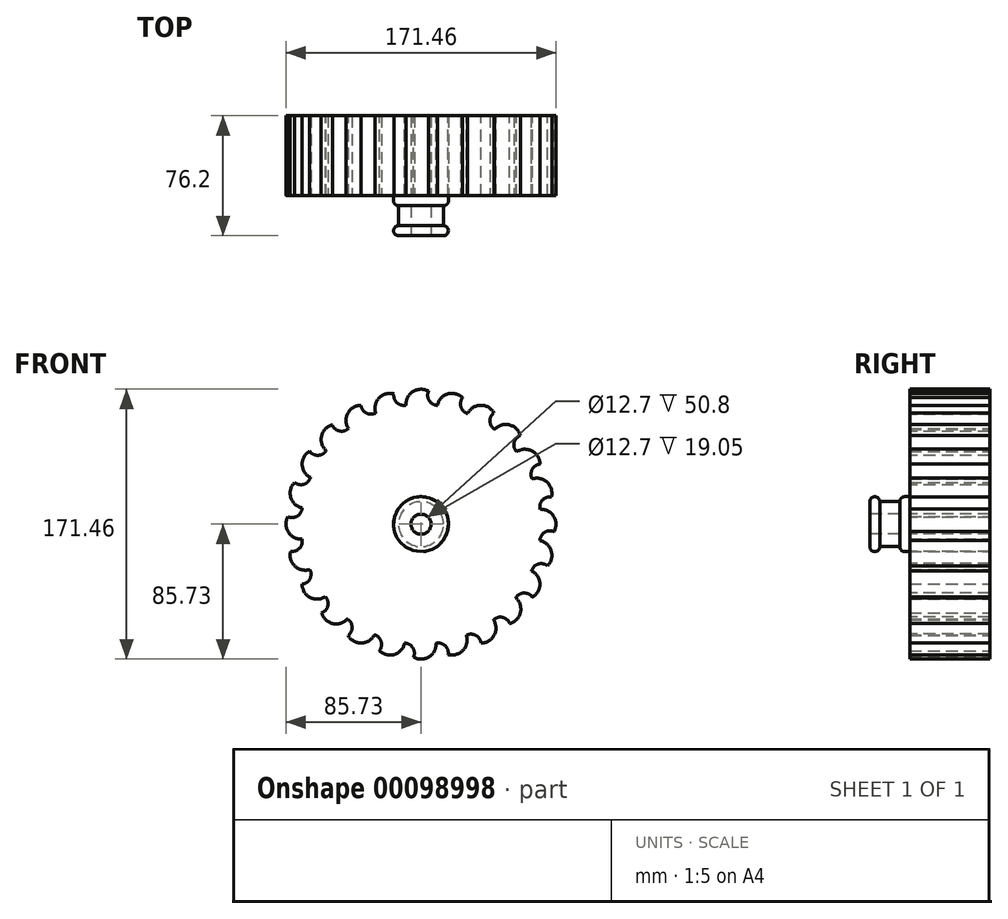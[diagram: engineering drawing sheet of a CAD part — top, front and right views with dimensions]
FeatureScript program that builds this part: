
annotation { "Feature Type Name" : "Feature", "Feature Type Description" : "" }
export const myFeature = defineFeature(function(context is Context, id is Id, definition is map)
    precondition{}
    {
        {
            var Q0;
            Q0=qCreatedBy(makeId("Front.planeOp"),FACE);
            var sketch = newSketch(context, id + "F0", { "sketchPlane" : qUnion([Q0])});
            skArc(sketch, "E0", {"start": v(-9.5, 75.6) * mm, "mid": v(4.76, -76.05) * mm, "end": v(0, 76.2) * mm});
            skArc(sketch, "E1", {"start": v(4.76, 84.45) * mm, "mid": v(-5.02, 84.3) * mm, "end": v(-9.5, 75.6) * mm});
            skLineSegment(sketch, "E2", {"start": v(0, 0) * mm, "end": v(0, 76.2) * mm, "construction": true});
            skLineSegment(sketch, "E3", {"start": v(0, 0) * mm, "end": v(39.83, 0) * mm, "construction": true});
            skLineSegment(sketch, "E4", {"start": v(0, 76.2) * mm, "end": v(4.76, 84.45) * mm});
            skArc(sketch, "E5.1.0", {"start": v(-17.26, 82.8) * mm, "mid": v(-26.66, 80.12) * mm, "end": v(-28.75, 70.57) * mm});
            skLineSegment(sketch, "E5.1.1", {"start": v(-19.72, 73.6) * mm, "end": v(-17.26, 82.8) * mm});
            skArc(sketch, "E5.2.0", {"start": v(-38.1, 75.52) * mm, "mid": v(-46.5, 70.5) * mm, "end": v(-46.04, 60.72) * mm});
            skLineSegment(sketch, "E5.2.1", {"start": v(-38.1, 66) * mm, "end": v(-38.1, 75.52) * mm});
            skArc(sketch, "E5.3.0", {"start": v(-56.35, 63.08) * mm, "mid": v(-63.15, 56.06) * mm, "end": v(-60.18, 46.74) * mm});
            skLineSegment(sketch, "E5.3.1", {"start": v(-53.88, 53.88) * mm, "end": v(-56.35, 63.08) * mm});
            skArc(sketch, "E5.4.0", {"start": v(-70.75, 46.35) * mm, "mid": v(-75.51, 37.8) * mm, "end": v(-70.23, 29.57) * mm});
            skLineSegment(sketch, "E5.4.1", {"start": v(-66, 38.1) * mm, "end": v(-70.75, 46.35) * mm});
            skArc(sketch, "E5.5.0", {"start": v(-80.34, 26.46) * mm, "mid": v(-82.72, 16.97) * mm, "end": v(-75.49, 10.39) * mm});
            skLineSegment(sketch, "E5.5.1", {"start": v(-73.6, 19.72) * mm, "end": v(-80.34, 26.46) * mm});
            skArc(sketch, "E5.6.0", {"start": v(-84.45, 4.76) * mm, "mid": v(-84.3, -5.02) * mm, "end": v(-75.6, -9.5) * mm});
            skLineSegment(sketch, "E5.6.1", {"start": v(-76.2, 0) * mm, "end": v(-84.45, 4.76) * mm});
            skArc(sketch, "E5.7.0", {"start": v(-82.8, -17.26) * mm, "mid": v(-80.12, -26.66) * mm, "end": v(-70.57, -28.75) * mm});
            skLineSegment(sketch, "E5.7.1", {"start": v(-73.6, -19.72) * mm, "end": v(-82.8, -17.26) * mm});
            skArc(sketch, "E5.8.0", {"start": v(-75.52, -38.1) * mm, "mid": v(-70.5, -46.5) * mm, "end": v(-60.72, -46.04) * mm});
            skLineSegment(sketch, "E5.8.1", {"start": v(-66, -38.1) * mm, "end": v(-75.52, -38.1) * mm});
            skArc(sketch, "E5.9.0", {"start": v(-63.08, -56.35) * mm, "mid": v(-56.06, -63.15) * mm, "end": v(-46.74, -60.18) * mm});
            skLineSegment(sketch, "E5.9.1", {"start": v(-53.88, -53.88) * mm, "end": v(-63.08, -56.35) * mm});
            skArc(sketch, "E5.10.0", {"start": v(-46.35, -70.75) * mm, "mid": v(-37.8, -75.51) * mm, "end": v(-29.57, -70.23) * mm});
            skLineSegment(sketch, "E5.10.1", {"start": v(-38.1, -66) * mm, "end": v(-46.35, -70.75) * mm});
            skArc(sketch, "E5.11.0", {"start": v(-26.46, -80.34) * mm, "mid": v(-16.97, -82.72) * mm, "end": v(-10.39, -75.49) * mm});
            skLineSegment(sketch, "E5.11.1", {"start": v(-19.72, -73.6) * mm, "end": v(-26.46, -80.34) * mm});
            skArc(sketch, "E5.12.0", {"start": v(-4.76, -84.45) * mm, "mid": v(5.02, -84.3) * mm, "end": v(9.5, -75.6) * mm});
            skLineSegment(sketch, "E5.12.1", {"start": v(0, -76.2) * mm, "end": v(-4.76, -84.45) * mm});
            skArc(sketch, "E5.13.0", {"start": v(17.26, -82.8) * mm, "mid": v(26.66, -80.12) * mm, "end": v(28.75, -70.57) * mm});
            skLineSegment(sketch, "E5.13.1", {"start": v(19.72, -73.6) * mm, "end": v(17.26, -82.8) * mm});
            skArc(sketch, "E5.14.0", {"start": v(38.1, -75.52) * mm, "mid": v(46.5, -70.5) * mm, "end": v(46.04, -60.72) * mm});
            skLineSegment(sketch, "E5.14.1", {"start": v(38.1, -66) * mm, "end": v(38.1, -75.52) * mm});
            skArc(sketch, "E5.15.0", {"start": v(56.35, -63.08) * mm, "mid": v(63.15, -56.06) * mm, "end": v(60.18, -46.74) * mm});
            skLineSegment(sketch, "E5.15.1", {"start": v(53.88, -53.88) * mm, "end": v(56.35, -63.08) * mm});
            skArc(sketch, "E5.16.0", {"start": v(70.75, -46.35) * mm, "mid": v(75.51, -37.8) * mm, "end": v(70.23, -29.57) * mm});
            skLineSegment(sketch, "E5.16.1", {"start": v(66, -38.1) * mm, "end": v(70.75, -46.35) * mm});
            skArc(sketch, "E5.17.0", {"start": v(80.34, -26.46) * mm, "mid": v(82.72, -16.97) * mm, "end": v(75.49, -10.39) * mm});
            skLineSegment(sketch, "E5.17.1", {"start": v(73.6, -19.72) * mm, "end": v(80.34, -26.46) * mm});
            skArc(sketch, "E5.18.0", {"start": v(84.45, -4.76) * mm, "mid": v(84.3, 5.02) * mm, "end": v(75.6, 9.5) * mm});
            skLineSegment(sketch, "E5.18.1", {"start": v(76.2, 0) * mm, "end": v(84.45, -4.76) * mm});
            skArc(sketch, "E5.19.0", {"start": v(82.8, 17.26) * mm, "mid": v(80.12, 26.66) * mm, "end": v(70.57, 28.75) * mm});
            skLineSegment(sketch, "E5.19.1", {"start": v(73.6, 19.72) * mm, "end": v(82.8, 17.26) * mm});
            skArc(sketch, "E5.20.0", {"start": v(75.52, 38.1) * mm, "mid": v(70.5, 46.5) * mm, "end": v(60.72, 46.04) * mm});
            skLineSegment(sketch, "E5.20.1", {"start": v(66, 38.1) * mm, "end": v(75.52, 38.1) * mm});
            skArc(sketch, "E5.21.0", {"start": v(63.08, 56.35) * mm, "mid": v(56.06, 63.15) * mm, "end": v(46.74, 60.18) * mm});
            skLineSegment(sketch, "E5.21.1", {"start": v(53.88, 53.88) * mm, "end": v(63.08, 56.35) * mm});
            skArc(sketch, "E5.22.0", {"start": v(46.35, 70.75) * mm, "mid": v(37.8, 75.51) * mm, "end": v(29.57, 70.23) * mm});
            skLineSegment(sketch, "E5.22.1", {"start": v(38.1, 66) * mm, "end": v(46.35, 70.75) * mm});
            skArc(sketch, "E5.23.0", {"start": v(26.46, 80.34) * mm, "mid": v(16.97, 82.72) * mm, "end": v(10.39, 75.49) * mm});
            skLineSegment(sketch, "E5.23.1", {"start": v(19.72, 73.6) * mm, "end": v(26.46, 80.34) * mm});
            skSolve(sketch);
        }
        {
            var Q0;
            Q0 = qSketchRegion(id + "F0", true);
            extrude(context, id + "F1", {"entities" : qUnion([Q0]), "depth" : 50.8 * mm});
        }
        {
            var Q0;
            Q0=makeQuery(id+"F1.opExtrude","CAP_FACE",FACE,{"disambiguationData":[OSD([sQuery(id+"F0.wireOp",EDGE,"E0"),sQuery(id+"F0.wireOp",EDGE,"E1"),sQuery(id+"F0.wireOp",EDGE,"E4"),sQuery(id+"F0.wireOp",EDGE,"E5.1.0"),sQuery(id+"F0.wireOp",EDGE,"E5.1.1"),sQuery(id+"F0.wireOp",EDGE,"E5.2.0"),sQuery(id+"F0.wireOp",EDGE,"E5.2.1"),sQuery(id+"F0.wireOp",EDGE,"E5.3.0"),sQuery(id+"F0.wireOp",EDGE,"E5.3.1"),sQuery(id+"F0.wireOp",EDGE,"E5.4.0"),sQuery(id+"F0.wireOp",EDGE,"E5.4.1"),sQuery(id+"F0.wireOp",EDGE,"E5.5.0"),sQuery(id+"F0.wireOp",EDGE,"E5.5.1"),sQuery(id+"F0.wireOp",EDGE,"E5.6.0"),sQuery(id+"F0.wireOp",EDGE,"E5.6.1"),sQuery(id+"F0.wireOp",EDGE,"E5.7.0"),sQuery(id+"F0.wireOp",EDGE,"E5.7.1"),sQuery(id+"F0.wireOp",EDGE,"E5.8.0"),sQuery(id+"F0.wireOp",EDGE,"E5.8.1"),sQuery(id+"F0.wireOp",EDGE,"E5.9.0"),sQuery(id+"F0.wireOp",EDGE,"E5.9.1"),sQuery(id+"F0.wireOp",EDGE,"E5.10.0"),sQuery(id+"F0.wireOp",EDGE,"E5.10.1"),sQuery(id+"F0.wireOp",EDGE,"E5.11.0"),sQuery(id+"F0.wireOp",EDGE,"E5.11.1"),sQuery(id+"F0.wireOp",EDGE,"E5.12.0"),sQuery(id+"F0.wireOp",EDGE,"E5.12.1"),sQuery(id+"F0.wireOp",EDGE,"E5.13.0"),sQuery(id+"F0.wireOp",EDGE,"E5.13.1"),sQuery(id+"F0.wireOp",EDGE,"E5.14.0"),sQuery(id+"F0.wireOp",EDGE,"E5.14.1"),sQuery(id+"F0.wireOp",EDGE,"E5.15.0"),sQuery(id+"F0.wireOp",EDGE,"E5.15.1"),sQuery(id+"F0.wireOp",EDGE,"E5.16.0"),sQuery(id+"F0.wireOp",EDGE,"E5.16.1"),sQuery(id+"F0.wireOp",EDGE,"E5.17.0"),sQuery(id+"F0.wireOp",EDGE,"E5.17.1"),sQuery(id+"F0.wireOp",EDGE,"E5.18.0"),sQuery(id+"F0.wireOp",EDGE,"E5.18.1"),sQuery(id+"F0.wireOp",EDGE,"E5.19.0"),sQuery(id+"F0.wireOp",EDGE,"E5.19.1"),sQuery(id+"F0.wireOp",EDGE,"E5.20.0"),sQuery(id+"F0.wireOp",EDGE,"E5.20.1"),sQuery(id+"F0.wireOp",EDGE,"E5.21.0"),sQuery(id+"F0.wireOp",EDGE,"E5.21.1"),sQuery(id+"F0.wireOp",EDGE,"E5.22.0"),sQuery(id+"F0.wireOp",EDGE,"E5.22.1"),sQuery(id+"F0.wireOp",EDGE,"E5.23.0"),sQuery(id+"F0.wireOp",EDGE,"E5.23.1")])],"isStart":false});
            var sketch = newSketch(context, id + "F2", { "sketchPlane" : qUnion([Q0])});
            skPoint(sketch, "E6", {"position": v(0, 0) * mm});
            skPoint(sketch, "E7", {"position": v(0, 0.1) * mm});
            skSolve(sketch);
        }
        {
            var Q0;
            Q0=sQuery(id+"F2.wireOp",VERTEX,"E6");
            var Q1;
            Q1=makeQuery(id+"F1.opExtrude","SWEPT_BODY",BODY,{"disambiguationData":[OSD([sQuery(id+"F0.wireOp",EDGE,"E0"),sQuery(id+"F0.wireOp",EDGE,"E1"),sQuery(id+"F0.wireOp",EDGE,"E4"),sQuery(id+"F0.wireOp",EDGE,"E5.1.0"),sQuery(id+"F0.wireOp",EDGE,"E5.1.1"),sQuery(id+"F0.wireOp",EDGE,"E5.2.0"),sQuery(id+"F0.wireOp",EDGE,"E5.2.1"),sQuery(id+"F0.wireOp",EDGE,"E5.3.0"),sQuery(id+"F0.wireOp",EDGE,"E5.3.1"),sQuery(id+"F0.wireOp",EDGE,"E5.4.0"),sQuery(id+"F0.wireOp",EDGE,"E5.4.1"),sQuery(id+"F0.wireOp",EDGE,"E5.5.0"),sQuery(id+"F0.wireOp",EDGE,"E5.5.1"),sQuery(id+"F0.wireOp",EDGE,"E5.6.0"),sQuery(id+"F0.wireOp",EDGE,"E5.6.1"),sQuery(id+"F0.wireOp",EDGE,"E5.7.0"),sQuery(id+"F0.wireOp",EDGE,"E5.7.1"),sQuery(id+"F0.wireOp",EDGE,"E5.8.0"),sQuery(id+"F0.wireOp",EDGE,"E5.8.1"),sQuery(id+"F0.wireOp",EDGE,"E5.9.0"),sQuery(id+"F0.wireOp",EDGE,"E5.9.1"),sQuery(id+"F0.wireOp",EDGE,"E5.10.0"),sQuery(id+"F0.wireOp",EDGE,"E5.10.1"),sQuery(id+"F0.wireOp",EDGE,"E5.11.0"),sQuery(id+"F0.wireOp",EDGE,"E5.11.1"),sQuery(id+"F0.wireOp",EDGE,"E5.12.0"),sQuery(id+"F0.wireOp",EDGE,"E5.12.1"),sQuery(id+"F0.wireOp",EDGE,"E5.13.0"),sQuery(id+"F0.wireOp",EDGE,"E5.13.1"),sQuery(id+"F0.wireOp",EDGE,"E5.14.0"),sQuery(id+"F0.wireOp",EDGE,"E5.14.1"),sQuery(id+"F0.wireOp",EDGE,"E5.15.0"),sQuery(id+"F0.wireOp",EDGE,"E5.15.1"),sQuery(id+"F0.wireOp",EDGE,"E5.16.0"),sQuery(id+"F0.wireOp",EDGE,"E5.16.1"),sQuery(id+"F0.wireOp",EDGE,"E5.17.0"),sQuery(id+"F0.wireOp",EDGE,"E5.17.1"),sQuery(id+"F0.wireOp",EDGE,"E5.18.0"),sQuery(id+"F0.wireOp",EDGE,"E5.18.1"),sQuery(id+"F0.wireOp",EDGE,"E5.19.0"),sQuery(id+"F0.wireOp",EDGE,"E5.19.1"),sQuery(id+"F0.wireOp",EDGE,"E5.20.0"),sQuery(id+"F0.wireOp",EDGE,"E5.20.1"),sQuery(id+"F0.wireOp",EDGE,"E5.21.0"),sQuery(id+"F0.wireOp",EDGE,"E5.21.1"),sQuery(id+"F0.wireOp",EDGE,"E5.22.0"),sQuery(id+"F0.wireOp",EDGE,"E5.22.1"),sQuery(id+"F0.wireOp",EDGE,"E5.23.0"),sQuery(id+"F0.wireOp",EDGE,"E5.23.1")])]});
            hole(context, id + "F3", {"style" : HoleStyle.SIMPLE, "endStyle" : HoleEndStyle.THROUGH, "holeDiameter" : 12.7 * mm, "locations" : qUnion([Q0]), "scope" : qUnion([Q1]), "isTappedThrough" : true});
        }
        {
            var Q0;
            Q0=makeQuery(id+"F1.opExtrude","CAP_FACE",FACE,{"disambiguationData":[OSD([sQuery(id+"F0.wireOp",EDGE,"E0"),sQuery(id+"F0.wireOp",EDGE,"E1"),sQuery(id+"F0.wireOp",EDGE,"E4"),sQuery(id+"F0.wireOp",EDGE,"E5.1.0"),sQuery(id+"F0.wireOp",EDGE,"E5.1.1"),sQuery(id+"F0.wireOp",EDGE,"E5.2.0"),sQuery(id+"F0.wireOp",EDGE,"E5.2.1"),sQuery(id+"F0.wireOp",EDGE,"E5.3.0"),sQuery(id+"F0.wireOp",EDGE,"E5.3.1"),sQuery(id+"F0.wireOp",EDGE,"E5.4.0"),sQuery(id+"F0.wireOp",EDGE,"E5.4.1"),sQuery(id+"F0.wireOp",EDGE,"E5.5.0"),sQuery(id+"F0.wireOp",EDGE,"E5.5.1"),sQuery(id+"F0.wireOp",EDGE,"E5.6.0"),sQuery(id+"F0.wireOp",EDGE,"E5.6.1"),sQuery(id+"F0.wireOp",EDGE,"E5.7.0"),sQuery(id+"F0.wireOp",EDGE,"E5.7.1"),sQuery(id+"F0.wireOp",EDGE,"E5.8.0"),sQuery(id+"F0.wireOp",EDGE,"E5.8.1"),sQuery(id+"F0.wireOp",EDGE,"E5.9.0"),sQuery(id+"F0.wireOp",EDGE,"E5.9.1"),sQuery(id+"F0.wireOp",EDGE,"E5.10.0"),sQuery(id+"F0.wireOp",EDGE,"E5.10.1"),sQuery(id+"F0.wireOp",EDGE,"E5.11.0"),sQuery(id+"F0.wireOp",EDGE,"E5.11.1"),sQuery(id+"F0.wireOp",EDGE,"E5.12.0"),sQuery(id+"F0.wireOp",EDGE,"E5.12.1"),sQuery(id+"F0.wireOp",EDGE,"E5.13.0"),sQuery(id+"F0.wireOp",EDGE,"E5.13.1"),sQuery(id+"F0.wireOp",EDGE,"E5.14.0"),sQuery(id+"F0.wireOp",EDGE,"E5.14.1"),sQuery(id+"F0.wireOp",EDGE,"E5.15.0"),sQuery(id+"F0.wireOp",EDGE,"E5.15.1"),sQuery(id+"F0.wireOp",EDGE,"E5.16.0"),sQuery(id+"F0.wireOp",EDGE,"E5.16.1"),sQuery(id+"F0.wireOp",EDGE,"E5.17.0"),sQuery(id+"F0.wireOp",EDGE,"E5.17.1"),sQuery(id+"F0.wireOp",EDGE,"E5.18.0"),sQuery(id+"F0.wireOp",EDGE,"E5.18.1"),sQuery(id+"F0.wireOp",EDGE,"E5.19.0"),sQuery(id+"F0.wireOp",EDGE,"E5.19.1"),sQuery(id+"F0.wireOp",EDGE,"E5.20.0"),sQuery(id+"F0.wireOp",EDGE,"E5.20.1"),sQuery(id+"F0.wireOp",EDGE,"E5.21.0"),sQuery(id+"F0.wireOp",EDGE,"E5.21.1"),sQuery(id+"F0.wireOp",EDGE,"E5.22.0"),sQuery(id+"F0.wireOp",EDGE,"E5.22.1"),sQuery(id+"F0.wireOp",EDGE,"E5.23.0"),sQuery(id+"F0.wireOp",EDGE,"E5.23.1")])],"isStart":false});
            var sketch = newSketch(context, id + "F4", { "sketchPlane" : qUnion([Q0])});
            skCircle(sketch, "E8", {"center": v(0, 0) * mm, "radius": 14.29 * mm});
            skSolve(sketch);
        }
        {
            var Q0;
            Q0=makeQuery(id+"F4.imprint","IMPRINT",FACE,{"disambiguationData":[TD([[makeQuery(id+"F4.imprint","IMPRINT",EDGE,{"derivedFrom":sQuery(id+"F4.wireOp",EDGE,"E8")}),1.0]])]});
            extrude(context, id + "F5", {"entities" : qUnion([Q0]), "operationType" : NewBodyOperationType.ADD, "depth" : 25.4 * mm});
        }
        {
            var Q0;
            Q0=makeQuery(id+"F1.opExtrude","CAP_FACE",FACE,{"disambiguationData":[OSD([sQuery(id+"F0.wireOp",EDGE,"E0"),sQuery(id+"F0.wireOp",EDGE,"E1"),sQuery(id+"F0.wireOp",EDGE,"E4"),sQuery(id+"F0.wireOp",EDGE,"E5.1.0"),sQuery(id+"F0.wireOp",EDGE,"E5.1.1"),sQuery(id+"F0.wireOp",EDGE,"E5.2.0"),sQuery(id+"F0.wireOp",EDGE,"E5.2.1"),sQuery(id+"F0.wireOp",EDGE,"E5.3.0"),sQuery(id+"F0.wireOp",EDGE,"E5.3.1"),sQuery(id+"F0.wireOp",EDGE,"E5.4.0"),sQuery(id+"F0.wireOp",EDGE,"E5.4.1"),sQuery(id+"F0.wireOp",EDGE,"E5.5.0"),sQuery(id+"F0.wireOp",EDGE,"E5.5.1"),sQuery(id+"F0.wireOp",EDGE,"E5.6.0"),sQuery(id+"F0.wireOp",EDGE,"E5.6.1"),sQuery(id+"F0.wireOp",EDGE,"E5.7.0"),sQuery(id+"F0.wireOp",EDGE,"E5.7.1"),sQuery(id+"F0.wireOp",EDGE,"E5.8.0"),sQuery(id+"F0.wireOp",EDGE,"E5.8.1"),sQuery(id+"F0.wireOp",EDGE,"E5.9.0"),sQuery(id+"F0.wireOp",EDGE,"E5.9.1"),sQuery(id+"F0.wireOp",EDGE,"E5.10.0"),sQuery(id+"F0.wireOp",EDGE,"E5.10.1"),sQuery(id+"F0.wireOp",EDGE,"E5.11.0"),sQuery(id+"F0.wireOp",EDGE,"E5.11.1"),sQuery(id+"F0.wireOp",EDGE,"E5.12.0"),sQuery(id+"F0.wireOp",EDGE,"E5.12.1"),sQuery(id+"F0.wireOp",EDGE,"E5.13.0"),sQuery(id+"F0.wireOp",EDGE,"E5.13.1"),sQuery(id+"F0.wireOp",EDGE,"E5.14.0"),sQuery(id+"F0.wireOp",EDGE,"E5.14.1"),sQuery(id+"F0.wireOp",EDGE,"E5.15.0"),sQuery(id+"F0.wireOp",EDGE,"E5.15.1"),sQuery(id+"F0.wireOp",EDGE,"E5.16.0"),sQuery(id+"F0.wireOp",EDGE,"E5.16.1"),sQuery(id+"F0.wireOp",EDGE,"E5.17.0"),sQuery(id+"F0.wireOp",EDGE,"E5.17.1"),sQuery(id+"F0.wireOp",EDGE,"E5.18.0"),sQuery(id+"F0.wireOp",EDGE,"E5.18.1"),sQuery(id+"F0.wireOp",EDGE,"E5.19.0"),sQuery(id+"F0.wireOp",EDGE,"E5.19.1"),sQuery(id+"F0.wireOp",EDGE,"E5.20.0"),sQuery(id+"F0.wireOp",EDGE,"E5.20.1"),sQuery(id+"F0.wireOp",EDGE,"E5.21.0"),sQuery(id+"F0.wireOp",EDGE,"E5.21.1"),sQuery(id+"F0.wireOp",EDGE,"E5.22.0"),sQuery(id+"F0.wireOp",EDGE,"E5.22.1"),sQuery(id+"F0.wireOp",EDGE,"E5.23.0"),sQuery(id+"F0.wireOp",EDGE,"E5.23.1")])],"isStart":false});
            var sketch = newSketch(context, id + "F6", { "sketchPlane" : qUnion([Q0])});
            skCircle(sketch, "E9", {"center": v(0, 0) * mm, "radius": 17.46 * mm});
            skSolve(sketch);
        }
        {
            var Q0;
            Q0 = qSketchRegion(id + "F6", true);
            extrude(context, id + "F7", {"entities" : qUnion([Q0]), "operationType" : NewBodyOperationType.ADD, "depth" : 6.35 * mm});
        }
        {
            var Q0;
            Q0=makeQuery(id+"F5.opExtrude","CAP_FACE",FACE,{"disambiguationData":[OSD([sQuery(id+"F3.hole-0.sketch.wireOp",EDGE,"core_line_2"),sQuery(id+"F3.hole-0.sketch.wireOp",EDGE,"core_line_3"),sQuery(id+"F4.wireOp",EDGE,"E8")])],"isStart":false});
            var sketch = newSketch(context, id + "F8", { "sketchPlane" : qUnion([Q0])});
            skCircle(sketch, "E10.0", {"center": v(0, 0) * mm, "radius": 17.46 * mm});
            skSolve(sketch);
        }
        {
            var Q0;
            Q0=makeQuery(id+"F8.imprint","IMPRINT",FACE,{"disambiguationData":[TD([[makeQuery(id+"F8.imprint","IMPRINT",EDGE,{"derivedFrom":sQuery(id+"F8.wireOp",EDGE,"E10.0")}),1.0]])]});
            extrude(context, id + "F9", {"entities" : qUnion([Q0]), "operationType" : NewBodyOperationType.ADD, "oppositeDirection" : true, "depth" : 6.35 * mm});
        }
        {
            var Q0;
            Q0=makeQuery(id+"F7.opExtrude","CAP_EDGE",EDGE,{"disambiguationData":[OSD([sQuery(id+"F6.wireOp",EDGE,"E9")])],"isStart":true});
            var Q1;
            Q1=makeQuery(id+"F9.opExtrude","CAP_EDGE",EDGE,{"disambiguationData":[OSD([sQuery(id+"F8.wireOp",EDGE,"E10.0")])],"isStart":true});
            var Q2;
            Q2=makeQuery(id+"F9.opExtrude","CAP_EDGE",EDGE,{"disambiguationData":[OSD([sQuery(id+"F8.wireOp",EDGE,"E10.0")])],"isStart":false});
            var Q3;
            Q3=makeQuery(id+"F7.opExtrude","CAP_EDGE",EDGE,{"disambiguationData":[OSD([sQuery(id+"F6.wireOp",EDGE,"E9")])],"isStart":false});
            fillet(context, id + "F10", {"entities" : qUnion([Q0, Q1, Q2, Q3]), "radius" : 3.17 * mm, "tangentPropagation" : true, "allowEdgeOverflow" : false});
        }
        {
            var Q0;
            Q0=makeQuery(id+"F1.opExtrude","SWEPT_EDGE",EDGE,{"disambiguationData":[OSD([sQuery(id+"F0.wireOp",EDGE,"E0"),sQuery(id+"F0.wireOp",EDGE,"E5.20.1")])]});
            var Q1;
            Q1=makeQuery(id+"F1.opExtrude","SWEPT_EDGE",EDGE,{"disambiguationData":[OSD([sQuery(id+"F0.wireOp",EDGE,"E0"),sQuery(id+"F0.wireOp",EDGE,"E5.21.1")])]});
            var Q2;
            Q2=makeQuery(id+"F1.opExtrude","SWEPT_EDGE",EDGE,{"disambiguationData":[OSD([sQuery(id+"F0.wireOp",EDGE,"E0"),sQuery(id+"F0.wireOp",EDGE,"E5.19.1")])]});
            var Q3;
            Q3=makeQuery(id+"F1.opExtrude","SWEPT_EDGE",EDGE,{"disambiguationData":[OSD([sQuery(id+"F0.wireOp",EDGE,"E0"),sQuery(id+"F0.wireOp",EDGE,"E5.18.1")])]});
            var Q4;
            Q4=makeQuery(id+"F1.opExtrude","SWEPT_EDGE",EDGE,{"disambiguationData":[OSD([sQuery(id+"F0.wireOp",EDGE,"E0"),sQuery(id+"F0.wireOp",EDGE,"E5.17.1")])]});
            var Q5;
            Q5=makeQuery(id+"F1.opExtrude","SWEPT_EDGE",EDGE,{"disambiguationData":[OSD([sQuery(id+"F0.wireOp",EDGE,"E0"),sQuery(id+"F0.wireOp",EDGE,"E5.16.1")])]});
            var Q6;
            Q6=makeQuery(id+"F1.opExtrude","SWEPT_EDGE",EDGE,{"disambiguationData":[OSD([sQuery(id+"F0.wireOp",EDGE,"E0"),sQuery(id+"F0.wireOp",EDGE,"E5.15.1")])]});
            var Q7;
            Q7=makeQuery(id+"F1.opExtrude","SWEPT_EDGE",EDGE,{"disambiguationData":[OSD([sQuery(id+"F0.wireOp",EDGE,"E0"),sQuery(id+"F0.wireOp",EDGE,"E5.14.1")])]});
            var Q8;
            Q8=makeQuery(id+"F1.opExtrude","SWEPT_EDGE",EDGE,{"disambiguationData":[OSD([sQuery(id+"F0.wireOp",EDGE,"E0"),sQuery(id+"F0.wireOp",EDGE,"E5.13.1")])]});
            var Q9;
            Q9=makeQuery(id+"F1.opExtrude","SWEPT_EDGE",EDGE,{"disambiguationData":[OSD([sQuery(id+"F0.wireOp",EDGE,"E0"),sQuery(id+"F0.wireOp",EDGE,"E5.12.1")])]});
            var Q10;
            Q10=makeQuery(id+"F1.opExtrude","SWEPT_EDGE",EDGE,{"disambiguationData":[OSD([sQuery(id+"F0.wireOp",EDGE,"E0"),sQuery(id+"F0.wireOp",EDGE,"E5.11.1")])]});
            var Q11;
            Q11=makeQuery(id+"F1.opExtrude","SWEPT_EDGE",EDGE,{"disambiguationData":[OSD([sQuery(id+"F0.wireOp",EDGE,"E0"),sQuery(id+"F0.wireOp",EDGE,"E5.10.1")])]});
            var Q12;
            Q12=makeQuery(id+"F1.opExtrude","SWEPT_EDGE",EDGE,{"disambiguationData":[OSD([sQuery(id+"F0.wireOp",EDGE,"E0"),sQuery(id+"F0.wireOp",EDGE,"E5.9.1")])]});
            var Q13;
            Q13=makeQuery(id+"F1.opExtrude","SWEPT_EDGE",EDGE,{"disambiguationData":[OSD([sQuery(id+"F0.wireOp",EDGE,"E0"),sQuery(id+"F0.wireOp",EDGE,"E5.8.1")])]});
            var Q14;
            Q14=makeQuery(id+"F1.opExtrude","SWEPT_EDGE",EDGE,{"disambiguationData":[OSD([sQuery(id+"F0.wireOp",EDGE,"E0"),sQuery(id+"F0.wireOp",EDGE,"E5.6.1")])]});
            var Q15;
            Q15=makeQuery(id+"F1.opExtrude","SWEPT_EDGE",EDGE,{"disambiguationData":[OSD([sQuery(id+"F0.wireOp",EDGE,"E0"),sQuery(id+"F0.wireOp",EDGE,"E5.7.1")])]});
            var Q16;
            Q16=makeQuery(id+"F1.opExtrude","SWEPT_EDGE",EDGE,{"disambiguationData":[OSD([sQuery(id+"F0.wireOp",EDGE,"E0"),sQuery(id+"F0.wireOp",EDGE,"E5.5.1")])]});
            var Q17;
            Q17=makeQuery(id+"F1.opExtrude","SWEPT_EDGE",EDGE,{"disambiguationData":[OSD([sQuery(id+"F0.wireOp",EDGE,"E0"),sQuery(id+"F0.wireOp",EDGE,"E5.4.1")])]});
            var Q18;
            Q18=makeQuery(id+"F1.opExtrude","SWEPT_EDGE",EDGE,{"disambiguationData":[OSD([sQuery(id+"F0.wireOp",EDGE,"E0"),sQuery(id+"F0.wireOp",EDGE,"E5.3.1")])]});
            var Q19;
            Q19=makeQuery(id+"F1.opExtrude","SWEPT_EDGE",EDGE,{"disambiguationData":[OSD([sQuery(id+"F0.wireOp",EDGE,"E0"),sQuery(id+"F0.wireOp",EDGE,"E5.1.1")])]});
            var Q20;
            Q20=makeQuery(id+"F1.opExtrude","SWEPT_EDGE",EDGE,{"disambiguationData":[OSD([sQuery(id+"F0.wireOp",EDGE,"E0"),sQuery(id+"F0.wireOp",EDGE,"E4")])]});
            var Q21;
            Q21=makeQuery(id+"F1.opExtrude","SWEPT_EDGE",EDGE,{"disambiguationData":[OSD([sQuery(id+"F0.wireOp",EDGE,"E0"),sQuery(id+"F0.wireOp",EDGE,"E5.2.1")])]});
            var Q22;
            Q22=makeQuery(id+"F1.opExtrude","SWEPT_EDGE",EDGE,{"disambiguationData":[OSD([sQuery(id+"F0.wireOp",EDGE,"E0"),sQuery(id+"F0.wireOp",EDGE,"E5.23.1")])]});
            var Q23;
            Q23=makeQuery(id+"F1.opExtrude","SWEPT_EDGE",EDGE,{"disambiguationData":[OSD([sQuery(id+"F0.wireOp",EDGE,"E0"),sQuery(id+"F0.wireOp",EDGE,"E5.22.1")])]});
            fillet(context, id + "F11", {"entities" : qUnion([Q0, Q1, Q2, Q3, Q4, Q5, Q6, Q7, Q8, Q9, Q10, Q11, Q12, Q13, Q14, Q15, Q16, Q17, Q18, Q19, Q20, Q21, Q22, Q23]), "radius" : 6.35 * mm, "tangentPropagation" : true, "allowEdgeOverflow" : false});
        }
    });
